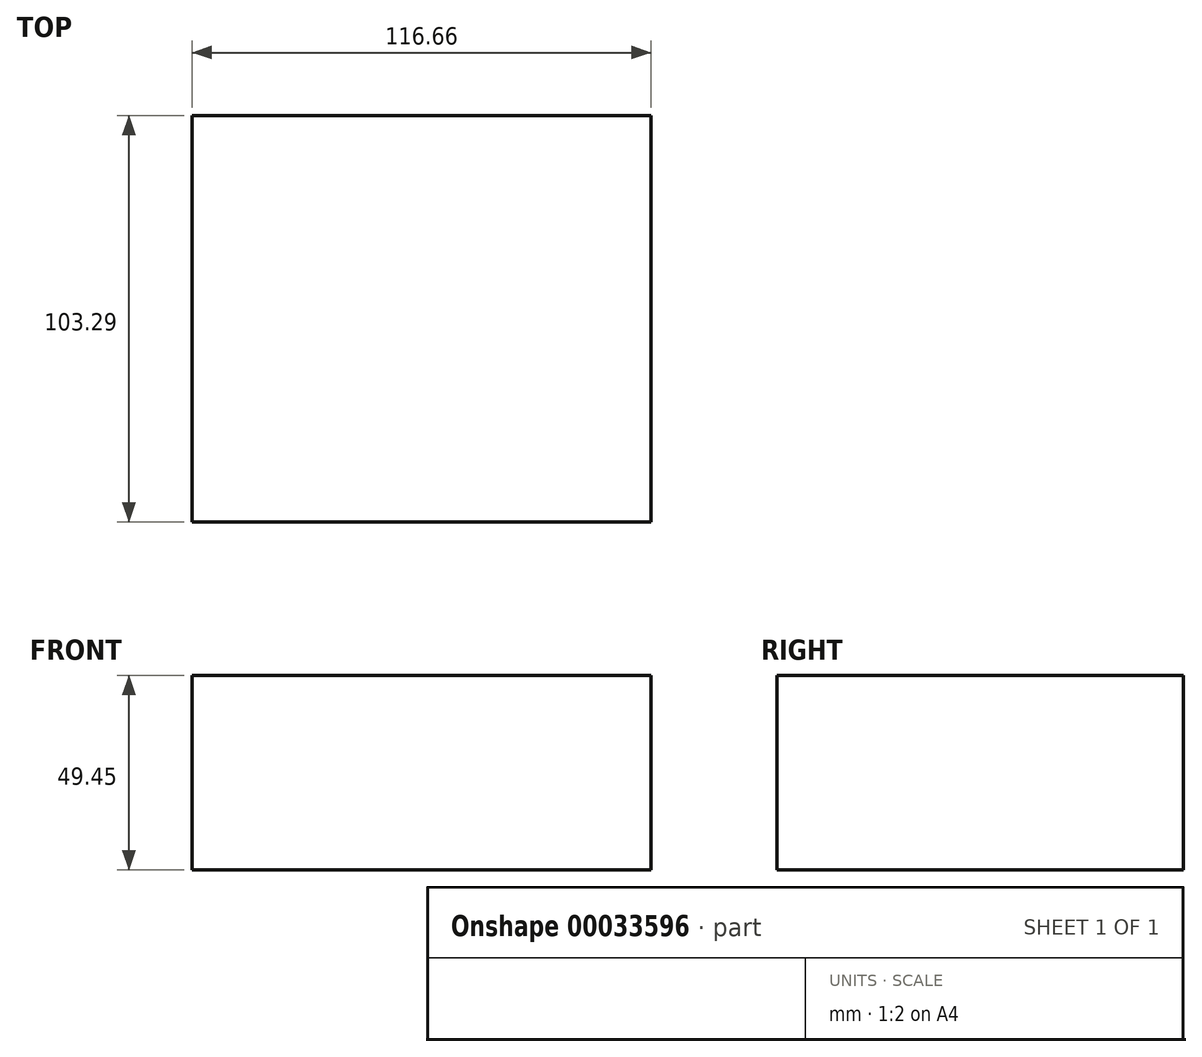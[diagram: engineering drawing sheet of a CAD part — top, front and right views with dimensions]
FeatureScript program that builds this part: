
annotation { "Feature Type Name" : "Feature", "Feature Type Description" : "" }
export const myFeature = defineFeature(function(context is Context, id is Id, definition is map)
    precondition{}
    {
        {
            var Q0;
            Q0=qCreatedBy(makeId("Top.planeOp"),FACE);
            var sketch = newSketch(context, id + "F0", { "sketchPlane" : qUnion([Q0])});
            skLineSegment(sketch, "E0.bottom", {"start": v(-58.05, 49.48) * mm, "end": v(58.6, 49.48) * mm});
            skLineSegment(sketch, "E0.top", {"start": v(-58.05, -53.81) * mm, "end": v(58.6, -53.81) * mm});
            skLineSegment(sketch, "E0.left", {"start": v(-58.05, 49.48) * mm, "end": v(-58.05, -53.81) * mm});
            skLineSegment(sketch, "E0.right", {"start": v(58.6, 49.48) * mm, "end": v(58.6, -53.81) * mm});
            skSolve(sketch);
        }
        {
            var Q0;
            Q0=makeQuery(id+"F0.imprint","IMPRINT",FACE,{"disambiguationData":[TD([[makeQuery(id+"F0.imprint","IMPRINT",EDGE,{"derivedFrom":sQuery(id+"F0.wireOp",EDGE,"E0.bottom")}),-1.0]])]});
            extrude(context, id + "F1", {"entities" : qUnion([Q0]), "depth" : 49.45 * mm});
        }
    });
